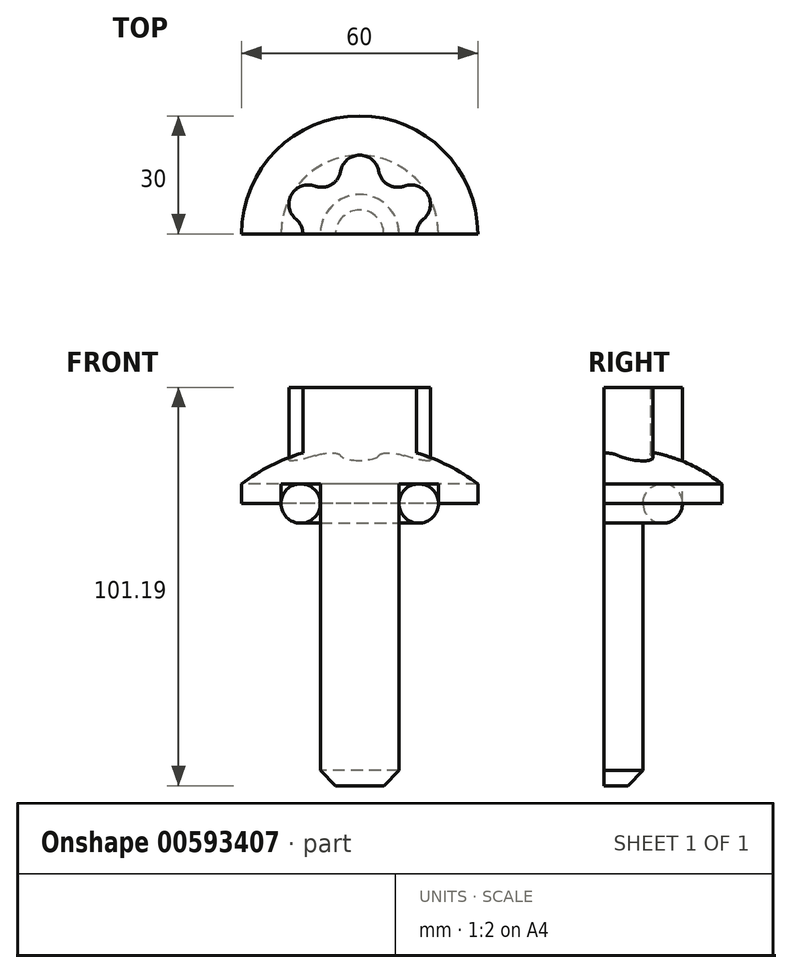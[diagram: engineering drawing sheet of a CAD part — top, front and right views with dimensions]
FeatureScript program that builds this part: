
annotation { "Feature Type Name" : "Feature", "Feature Type Description" : "" }
export const myFeature = defineFeature(function(context is Context, id is Id, definition is map)
    precondition{}
    {
        {
            var Q0;
            Q0=qCreatedBy(makeId("Front.planeOp"),FACE);
            var sketch = newSketch(context, id + "F0", { "sketchPlane" : qUnion([Q0])});
            skLineSegment(sketch, "E0", {"start": v(0, -48.02) * mm, "end": v(0, 38.67) * mm});
            skLineSegment(sketch, "E1", {"start": v(-30, 28.67) * mm, "end": v(-30, 23.67) * mm});
            skLineSegment(sketch, "E2", {"start": v(-30, 23.67) * mm, "end": v(-20, 23.67) * mm});
            skLineSegment(sketch, "E3", {"start": v(-20, 23.67) * mm, "end": v(-20, 28.67) * mm});
            skLineSegment(sketch, "E4", {"start": v(-20, 28.67) * mm, "end": v(-10, 28.67) * mm});
            skLineSegment(sketch, "E5", {"start": v(-10, 28.67) * mm, "end": v(-10, -44.13) * mm});
            skLineSegment(sketch, "E6", {"start": v(-10, -44.13) * mm, "end": v(-6.11, -48.02) * mm});
            skLineSegment(sketch, "E7", {"start": v(-6.11, -48.02) * mm, "end": v(0, -48.02) * mm});
            skArc(sketch, "E8", {"start": v(0, 38.67) * mm, "mid": v(-15.81, 36.1) * mm, "end": v(-30, 28.67) * mm});
            skPoint(sketch, "E9.orphan", {"position": v(0, 48.93) * mm});
            skPoint(sketch, "E10.orphan", {"position": v(30, 28.67) * mm});
            skSolve(sketch);
        }
        {
            var Q0;
            Q0=makeQuery(id+"F0.imprint","IMPRINT",FACE,{"disambiguationData":[TD([[makeQuery(id+"F0.imprint","IMPRINT",EDGE,{"derivedFrom":sQuery(id+"F0.wireOp",EDGE,"E0")}),1.0]])]});
            var Q1;
            Q1=sQuery(id+"F0.wireOp",EDGE,"E0");
            revolve(context, id + "F1", {"surfaceOperationType" : NewSurfaceOperationType.NEW, "entities" : qUnion([Q0]), "axis" : qUnion([Q1]), "revolveType" : RevolveType.ONE_DIRECTION, "oppositeDirection" : true, "angle" : 180 * degree});
        }
        {
            var Q0;
            Q0=makeQuery(id+"F1.opRevolve","SWEPT_FACE",FACE,{"disambiguationData":[OSD([sQuery(id+"F0.wireOp",EDGE,"E4")])]});
            var sketch = newSketch(context, id + "F2", { "sketchPlane" : qUnion([Q0])});
            skCircle(sketch, "E11", {"center": v(0, 0) * mm, "radius": 20 * mm, "construction": true});
            skLineSegment(sketch, "E12", {"start": v(0, 0) * mm, "end": v(0, -20) * mm, "construction": true});
            skLineSegment(sketch, "E13", {"start": v(0, 0) * mm, "end": v(17.32, -10) * mm, "construction": true});
            skArc(sketch, "E14", {"start": v(0, -20) * mm, "mid": v(3.16, -18.85) * mm, "end": v(4.84, -15.93) * mm});
            skArc(sketch, "E15", {"start": v(11.37, -12.15) * mm, "mid": v(14.74, -12.16) * mm, "end": v(17.32, -10) * mm});
            skArc(sketch, "E16.trimOffspring", {"start": v(11.37, -12.15) * mm, "mid": v(7.22, -12.5) * mm, "end": v(4.84, -15.93) * mm});
            skArc(sketch, "E17.1.0", {"start": v(17.32, -10) * mm, "mid": v(17.9, -6.68) * mm, "end": v(16.21, -3.77) * mm});
            skArc(sketch, "E17.1.1", {"start": v(14.44, 0) * mm, "mid": v(14.9, -2.08) * mm, "end": v(16.21, -3.77) * mm});
            skArc(sketch, "E17.1.2", {"start": v(16.21, 3.77) * mm, "mid": v(17.9, 6.68) * mm, "end": v(17.32, 10) * mm});
            skArc(sketch, "E17.2.0", {"start": v(17.32, 10) * mm, "mid": v(14.74, 12.16) * mm, "end": v(11.37, 12.15) * mm});
            skArc(sketch, "E17.2.1", {"start": v(4.84, 15.93) * mm, "mid": v(7.22, 12.5) * mm, "end": v(11.37, 12.15) * mm});
            skArc(sketch, "E17.2.2", {"start": v(4.84, 15.93) * mm, "mid": v(3.16, 18.85) * mm, "end": v(0, 20) * mm});
            skArc(sketch, "E17.3.0", {"start": v(0, 20) * mm, "mid": v(-3.16, 18.85) * mm, "end": v(-4.84, 15.93) * mm});
            skArc(sketch, "E17.3.1", {"start": v(-11.37, 12.15) * mm, "mid": v(-7.22, 12.5) * mm, "end": v(-4.84, 15.93) * mm});
            skArc(sketch, "E17.3.2", {"start": v(-11.37, 12.15) * mm, "mid": v(-14.74, 12.16) * mm, "end": v(-17.32, 10) * mm});
            skArc(sketch, "E17.4.0", {"start": v(-17.32, 10) * mm, "mid": v(-17.9, 6.68) * mm, "end": v(-16.21, 3.77) * mm});
            skArc(sketch, "E17.4.1", {"start": v(-16.21, -3.77) * mm, "mid": v(-14.9, -2.08) * mm, "end": v(-14.44, 0) * mm});
            skArc(sketch, "E17.4.2", {"start": v(-16.21, -3.77) * mm, "mid": v(-17.9, -6.68) * mm, "end": v(-17.32, -10) * mm});
            skArc(sketch, "E17.5.0", {"start": v(-17.32, -10) * mm, "mid": v(-14.74, -12.16) * mm, "end": v(-11.37, -12.15) * mm});
            skArc(sketch, "E17.5.1", {"start": v(-4.84, -15.93) * mm, "mid": v(-7.22, -12.5) * mm, "end": v(-11.37, -12.15) * mm});
            skArc(sketch, "E17.5.2", {"start": v(-4.84, -15.93) * mm, "mid": v(-3.16, -18.85) * mm, "end": v(0, -20) * mm});
            skLineSegment(sketch, "E18.trimOffspring", {"start": v(-14.44, 0) * mm, "end": v(14.44, 0) * mm});
            skSolve(sketch);
        }
        {
            var Q0;
            Q0 = qSketchRegion(id + "F2", true);
            extrude(context, id + "F3", {"entities" : qUnion([Q0]), "operationType" : NewBodyOperationType.ADD, "oppositeDirection" : true, "depth" : 24.5 * mm, "offsetDistance" : 25 * mm});
        }
        {
            var Q0;
            Q0=makeQuery(id+"F3.boolean.opBoolean","MERGE",FACE,{"derivedFrom":[makeQuery(id+"F1.opRevolve","CAP_FACE",FACE,{"disambiguationData":[OSD([sQuery(id+"F0.wireOp",EDGE,"E0"),sQuery(id+"F0.wireOp",EDGE,"E1"),sQuery(id+"F0.wireOp",EDGE,"E2"),sQuery(id+"F0.wireOp",EDGE,"E3"),sQuery(id+"F0.wireOp",EDGE,"E4"),sQuery(id+"F0.wireOp",EDGE,"E5"),sQuery(id+"F0.wireOp",EDGE,"E6"),sQuery(id+"F0.wireOp",EDGE,"E7"),sQuery(id+"F0.wireOp",EDGE,"E8")])],"isStart":false}),makeQuery(id+"F3.opExtrude","SWEPT_FACE",FACE,{"disambiguationData":[OSD([sQuery(id+"F2.wireOp",EDGE,"E18.trimOffspring")])]})]});
            var sketch = newSketch(context, id + "F4", { "sketchPlane" : qUnion([Q0])});
            skCircle(sketch, "E19", {"center": v(-15, 23.67) * mm, "radius": 5 * mm});
            skSolve(sketch);
        }
        {
            var Q0;
            {var subQ0=sQuery(id+"F4.wireOp",EDGE,"E19");var subQ1=makeQuery(id+"F4.imprint","INTERSECT",VERTEX,{"derivedFrom":[makeQuery(id+"F1.opRevolve","CAP_EDGE",EDGE,{"disambiguationData":[OSD([sQuery(id+"F0.wireOp",EDGE,"E5")])],"isStart":true}),subQ0]});Q0=makeQuery(id+"F4.imprint","IMPRINT",FACE,{"disambiguationData":[TD([[makeQuery(id+"F4.imprint","IMPRINT",EDGE,{"disambiguationData":[TD([[subQ1,-1.0]])],"derivedFrom":subQ0}),1.0]])]});}
            var Q1;
            Q1=makeQuery(id+"F1.opRevolve","SWEPT_FACE",FACE,{"disambiguationData":[OSD([sQuery(id+"F0.wireOp",EDGE,"E3")])]});
            revolve(context, id + "F5", {"surfaceOperationType" : NewSurfaceOperationType.NEW, "entities" : qUnion([Q0]), "axis" : qUnion([Q1]), "revolveType" : RevolveType.ONE_DIRECTION, "angle" : 180 * degree});
        }
    });
